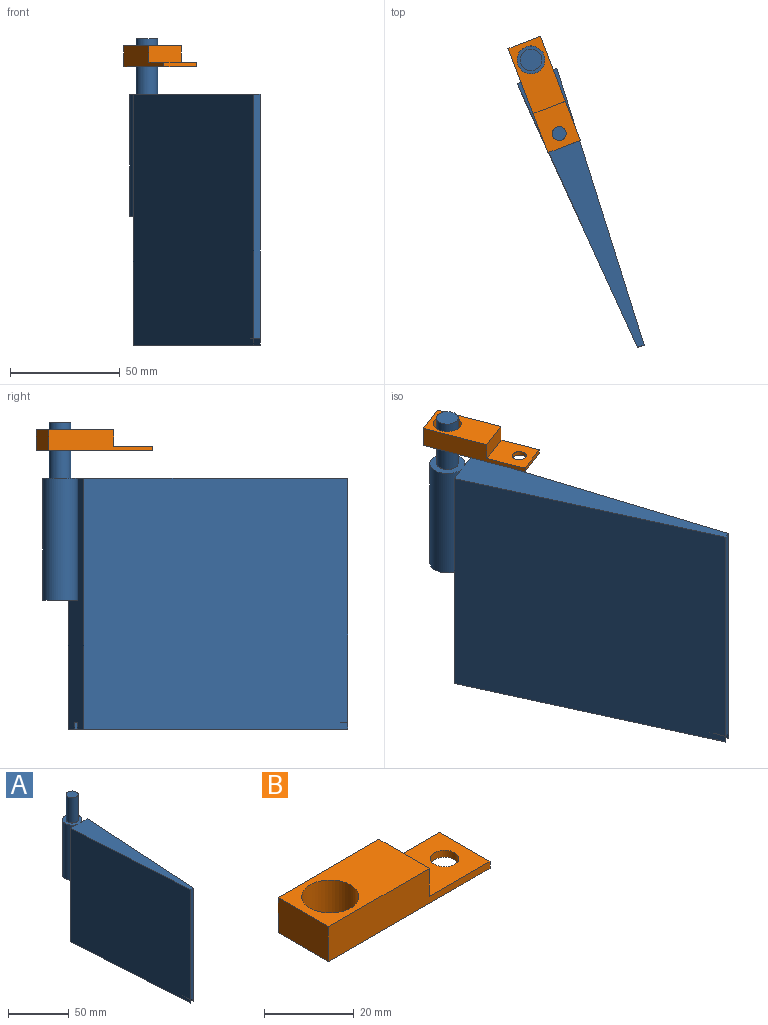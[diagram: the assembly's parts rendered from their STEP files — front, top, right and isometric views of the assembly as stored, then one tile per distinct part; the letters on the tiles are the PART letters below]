
ASSEMBLY  parts=2 mates=1
PART A: 16 faces, bbox 19.4x147.6x139.7 mm
  f0: plane 15.88x15.71mm, normal (0,0,-1), area 126.3mm2, adj f1,f3,f5
  f1: cylinder r=7.94mm len=55.56mm, axis (0,0,-1), area 2593.4mm2, adj f0,f4,f5
  f2: plane 111.13x3.18mm, normal (0,-1,0), area 352.8mm2, adj f4,f6,f8,f11
  f3: cylinder r=4.76mm len=55.56mm, axis (0,0,-1), area 1662.6mm2, adj f0,f15
  f4: plane 147.64x19.43mm, normal (0,0,1), area 1612.4mm2, adj f1,f2,f5,f8,f11,f14
  f5: plane 114.3x19.43mm, normal (0,1,0), area 2034.5mm2, adj f0,f1,f4,f6,f7,f8,f9,f10
  f6: plane 131.92x3.18mm, normal (0,0,-1), area 418.9mm2, adj f2,f5,f7,f10
  f7: plane 131.92x3.18mm, normal (1,0,0), area 418.9mm2, adj f5,f6,f8,f9
  f8: plane 131.92x114.3mm, normal (-1,-0.06,0), area 15107.4mm2, adj f2,f4,f5,f7,f9
  f9: plane 131.92x8.13mm, normal (0,0,-1), area 536.1mm2, adj f5,f7,f8
  f10: plane 131.92x3.18mm, normal (-1,0,0), area 418.9mm2, adj f5,f6,f11,f12
  f11: plane 131.92x114.3mm, normal (1,-0.06,0), area 15107.4mm2, adj f2,f4,f5,f10,f12
  f12: plane 131.92x8.13mm, normal (0,0,-1), area 536.1mm2, adj f5,f10,f11
  f13: plane 9.86x9.86mm, normal (0,0,1), area 76.3mm2, adj f14
  f14: cylinder r=4.93mm len=25.4mm, axis (0,0,-1), area 786.5mm2, adj f4,f13
  f15: plane 9.53x9.53mm, normal (0,0,-1), area 71.3mm2, adj f3
PART B: 10 faces, bbox 50.8x15.9x9.5 mm
  f0: plane 15.88x1.91mm, normal (1,0,0), area 30.2mm2, adj f1,f2,f6,f8
  f1: plane 50.8x9.53mm, normal (0,-1,0), area 338.7mm2, adj f0,f4,f5,f6,f7,f8
  f2: plane 50.8x9.53mm, normal (0,1,0), area 338.7mm2, adj f0,f4,f5,f6,f7,f8
  f3: cylinder r=6.35mm len=12.7mm, axis (0,0,-1), area 380mm2, adj f5,f6
  f4: plane 15.88x9.53mm, normal (-1,0,0), area 151.2mm2, adj f1,f2,f5,f6
  f5: plane 31.75x15.88mm, normal (0,0,1), area 377.4mm2, adj f1,f2,f3,f4,f7
  f6: plane 50.8x15.88mm, normal (0,0,-1), area 648.1mm2, adj f0,f1,f2,f3,f4,f9
  f7: plane 15.88x7.62mm, normal (1,0,0), area 121mm2, adj f1,f2,f5,f8
  f8: plane 19.05x15.88mm, normal (0,0,1), area 270.7mm2, adj f0,f1,f2,f7,f9
  f9: cylinder r=3.17mm len=6.35mm, axis (0,0,1), area 38mm2, adj f6,f8
PLACE A rot(axis=(0,0,1),21deg) t=(-52.97,85.56,62.38)mm
PLACE B rot(axis=(0,0,-1),69deg) t=(-52.97,85.56,130.64)mm
MATE fastened B.f3 <-> A.f1  axis (0,0,-1) through (-52.97,85.56,130.64)mm
